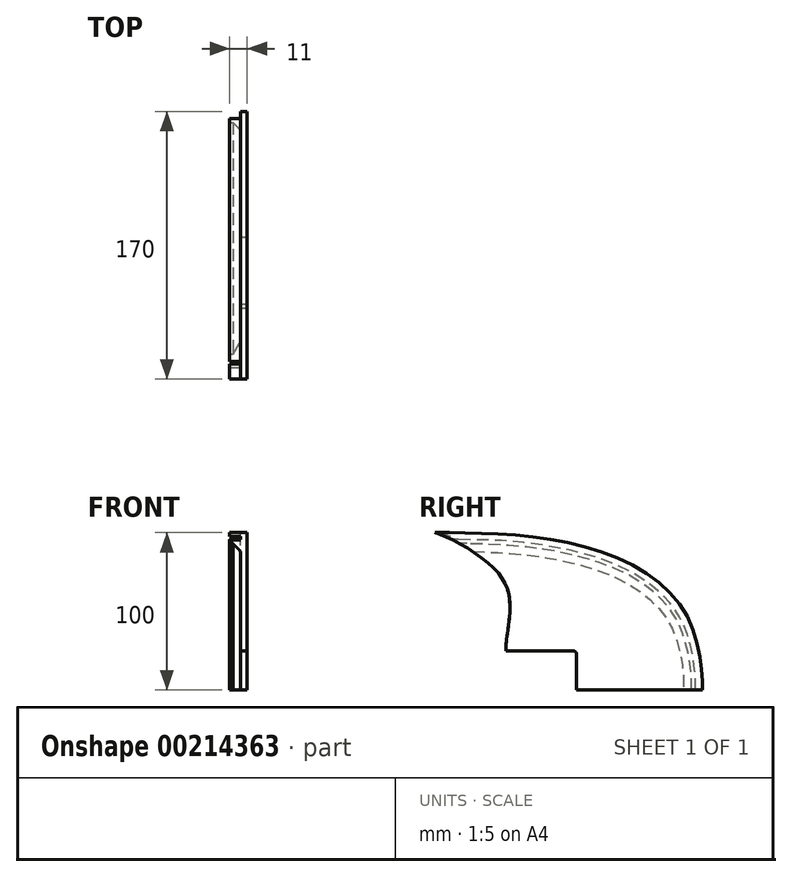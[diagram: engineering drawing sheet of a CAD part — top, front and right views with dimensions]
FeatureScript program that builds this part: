
annotation { "Feature Type Name" : "Feature", "Feature Type Description" : "" }
export const myFeature = defineFeature(function(context is Context, id is Id, definition is map)
    precondition{}
    {
        {
            var Q0;
            Q0=qCreatedBy(makeId("Right.planeOp"),FACE);
            var sketch = newSketch(context, id + "F0", { "sketchPlane" : qUnion([Q0])});
            skLineSegment(sketch, "E0", {"start": v(0, 0) * mm, "end": v(80, 0) * mm});
            skLineSegment(sketch, "E1", {"start": v(0, 0) * mm, "end": v(0, 25) * mm});
            skLineSegment(sketch, "E2", {"start": v(0, 25) * mm, "end": v(-45, 25) * mm});
            skFitSpline(sketch, "E3", {"points": [v(-45, 25) * mm, v(-42.34, 54.32) * mm, v(-53.59, 78.31) * mm, v(-90, 100) * mm], "startDerivative": vector(0, 72.19) * mm, "endDerivative": vector(-68.17, 16.6) * mm});
            skFitSpline(sketch, "E4", {"points": [v(80, 0) * mm, v(68.23, 50.32) * mm, v(0, 92.35) * mm, v(-90, 100) * mm], "startDerivative": vector(0, 120.91) * mm, "endDerivative": vector(-206.88, 0) * mm});
            skLineSegment(sketch, "E5", {"start": v(80, 0) * mm, "end": v(80, 46.96) * mm, "construction": true});
            skLineSegment(sketch, "E6", {"start": v(-90, 100) * mm, "end": v(-41.9, 100) * mm, "construction": true});
            skLineSegment(sketch, "E7", {"start": v(-45, 25) * mm, "end": v(-45, 57.26) * mm, "construction": true});
            skSolve(sketch);
        }
        {
            var Q0;
            Q0=makeQuery(id+"F0.imprint","IMPRINT",FACE,{"disambiguationData":[TD([[makeQuery(id+"F0.imprint","IMPRINT",EDGE,{"derivedFrom":sQuery(id+"F0.wireOp",EDGE,"E0")}),1.0]])]});
            extrude(context, id + "F1", {"entities" : qUnion([Q0]), "depth" : 4 * mm});
        }
        {
            var Q0;
            Q0=makeQuery(id+"F1.opExtrude","SWEPT_EDGE",EDGE,{"disambiguationData":[OSD([sQuery(id+"F0.wireOp",EDGE,"E1"),sQuery(id+"F0.wireOp",EDGE,"E2")])]});
            fillet(context, id + "F2", {"entities" : qUnion([Q0]), "radius" : 2.5 * mm, "tangentPropagation" : true, "allowEdgeOverflow" : false});
        }
        {
            var Q0;
            Q0=makeQuery(id+"F1.opExtrude","CAP_FACE",FACE,{"disambiguationData":[OSD([sQuery(id+"F0.wireOp",EDGE,"E0"),sQuery(id+"F0.wireOp",EDGE,"E1"),sQuery(id+"F0.wireOp",EDGE,"E2"),sQuery(id+"F0.wireOp",EDGE,"E3"),sQuery(id+"F0.wireOp",EDGE,"E4")])],"isStart":true});
            var sketch = newSketch(context, id + "F3", { "sketchPlane" : qUnion([Q0])});
            skFitSpline(sketch, "E8.0", {"points": [v(-77.5, 0) * mm, v(-77.5, 2.47) * mm, v(-77.35, 8.46) * mm, v(-76.41, 17.69) * mm, v(-74.97, 25.59) * mm, v(-73.49, 31.64) * mm, v(-71.55, 37.7) * mm, v(-69.5, 42.62) * mm, v(-67.6, 46.43) * mm, v(-66.02, 49.2) * mm, v(-64.28, 51.9) * mm, v(-61.76, 55.37) * mm, v(-58.24, 59.5) * mm, v(-53.45, 64.15) * mm, v(-48.15, 68.47) * mm, v(-40.46, 73.8) * mm, v(-29.77, 79.65) * mm, v(-15.64, 85.39) * mm, v(-0.58, 89.86) * mm, v(15.03, 93.08) * mm, v(36.16, 95.98) * mm, v(62.35, 97.47) * mm, v(81.38, 97.5) * mm, v(90, 97.5) * mm]});
            skFitSpline(sketch, "E9.0", {"points": [v(-75.5, 0) * mm, v(-75.5, 2.43) * mm, v(-75.36, 8.33) * mm, v(-74.43, 17.42) * mm, v(-73.01, 25.17) * mm, v(-71.56, 31.1) * mm, v(-69.67, 37) * mm, v(-67.68, 41.8) * mm, v(-65.83, 45.5) * mm, v(-64.3, 48.17) * mm, v(-62.63, 50.76) * mm, v(-60.2, 54.12) * mm, v(-56.78, 58.13) * mm, v(-52.13, 62.65) * mm, v(-46.95, 66.86) * mm, v(-39.42, 72.08) * mm, v(-28.92, 77.83) * mm, v(-14.98, 83.5) * mm, v(-2.57, 87.18) * mm, v(7.63, 89.51) * mm, v(17.99, 91.47) * mm, v(36.33, 93.98) * mm, v(62.4, 95.47) * mm, v(81.38, 95.5) * mm, v(90, 95.5) * mm]});
            skFitSpline(sketch, "E10.0", {"points": [v(-73, 0) * mm, v(-73, 2.38) * mm, v(-72.86, 8.17) * mm, v(-71.95, 17.08) * mm, v(-70.57, 24.65) * mm, v(-69.15, 30.43) * mm, v(-67.62, 35.2) * mm, v(-66.17, 38.92) * mm, v(-64.96, 41.66) * mm, v(-63.85, 43.87) * mm, v(-62.9, 45.6) * mm, v(-61.9, 47.28) * mm, v(-60.57, 49.35) * mm, v(-58.82, 51.76) * mm, v(-56.93, 54.1) * mm, v(-54.2, 57.14) * mm, v(-50.47, 60.77) * mm, v(-45.45, 64.86) * mm, v(-38.12, 69.94) * mm, v(-27.86, 75.56) * mm, v(-16.45, 80.2) * mm, v(-6.82, 83.3) * mm, v(0.59, 85.34) * mm, v(8.14, 87.06) * mm, v(18.38, 89) * mm, v(31.36, 90.78) * mm, v(46.92, 92.08) * mm, v(67.19, 92.98) * mm, v(81.39, 93) * mm, v(90, 93) * mm]});
            skFitSpline(sketch, "E11.0", {"points": [v(45, 25) * mm, v(45, 32.64) * mm, v(39.33, 55.94) * mm, v(49.57, 79.91) * mm, v(81.34, 97.9) * mm, v(90, 100) * mm]});
            skLineSegment(sketch, "E12.0", {"start": v(-73, 0) * mm, "end": v(-75.5, 0) * mm});
            skPoint(sketch, "E13.orphan", {"position": v(45, 25) * mm});
            skPoint(sketch, "E14.orphan", {"position": v(0, 0) * mm});
            skLineSegment(sketch, "E15.trimOffspring", {"start": v(-77.5, 0) * mm, "end": v(-80, 0) * mm});
            skFitSpline(sketch, "E16.0", {"points": [v(-80, 0) * mm, v(-80, 11.3) * mm, v(-76.66, 60.6) * mm, v(-0.93, 99.77) * mm, v(64.44, 100) * mm, v(90, 100) * mm]});
            skFitSpline(sketch, "E17.0", {"points": [v(45, 25) * mm, v(45, 32.64) * mm, v(39.33, 55.94) * mm, v(49.57, 79.91) * mm, v(81.34, 97.9) * mm, v(90, 100) * mm]});
            skFitSpline(sketch, "E18.trimOffspring", {"points": [v(45, 25) * mm, v(45, 32.64) * mm, v(39.33, 55.94) * mm, v(49.57, 79.91) * mm, v(81.34, 97.9) * mm, v(90, 100) * mm]});
            skSolve(sketch);
        }
        {
            var Q0;
            Q0=makeQuery(id+"F3.imprint","IMPRINT",FACE,{"disambiguationData":[TD([[makeQuery(id+"F3.imprint","IMPRINT",EDGE,{"derivedFrom":sQuery(id+"F3.wireOp",EDGE,"E8.0")}),1.0]])]});
            var Q1;
            Q1=makeQuery(id+"F3.imprint","IMPRINT",FACE,{"disambiguationData":[TD([[makeQuery(id+"F3.imprint","IMPRINT",EDGE,{"derivedFrom":sQuery(id+"F3.wireOp",EDGE,"E9.0")}),-1.0]])]});
            extrude(context, id + "F4", {"entities" : qUnion([Q0, Q1]), "operationType" : NewBodyOperationType.ADD, "depth" : 7 * mm});
        }
        {
            var Q0;
            Q0=makeQuery(id+"F4.opExtrude","CAP_EDGE",EDGE,{"disambiguationData":[OSD([sQuery(id+"F3.wireOp",EDGE,"E10.0")])],"isStart":true});
            chamfer(context, id + "F5", {"entities" : qUnion([Q0]), "width" : 5 * mm, "tangentPropagation" : true});
        }
    });
